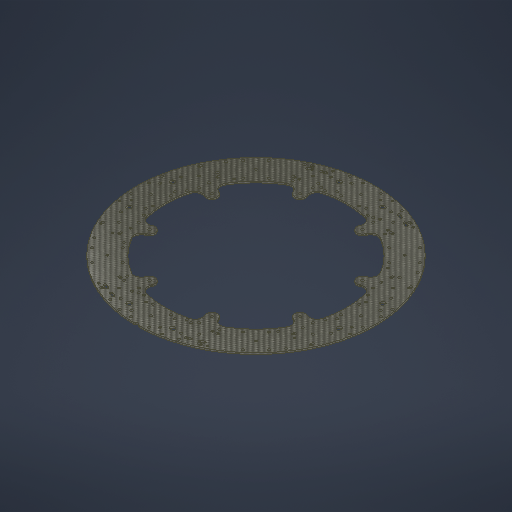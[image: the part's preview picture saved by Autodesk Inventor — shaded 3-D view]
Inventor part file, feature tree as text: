
AUTODESK INVENTOR PART (.ipt)
format: ipt  version: 2025 (Build 290162010, 162A)  size: 835,584 bytes
history: native  units: mm
features: extrude x1, sketch x1
ambient origin geometry x8: Origin, YZ Plane, XZ Plane, XY Plane, X Axis, Y Axis, Z Axis, Center Point
bodies: Solid1 (feature_tree)
feature tree (2):
  extrude  "Extrusion1"  [1 undecoded]
  sketch  "Sketch1"  dims[d0=2.0mm d1=0.0mm]
note: 1 required parameter value undecoded (feature->parameter linkage not recoverable at this tier; creation-order binding heuristic only, values carry confidence <= 0.55)
